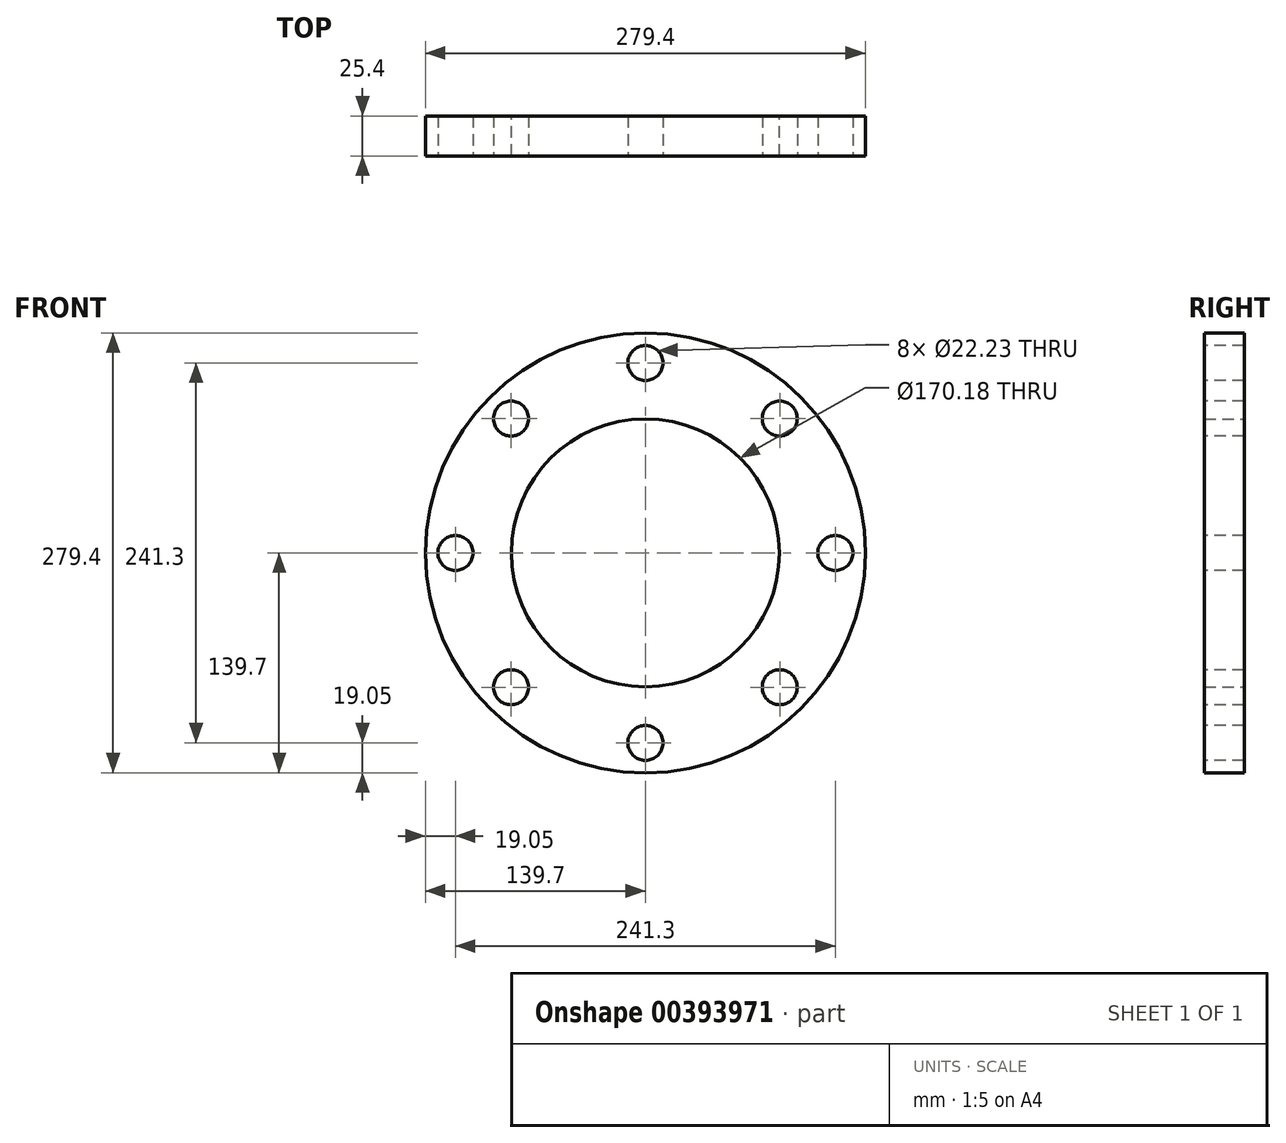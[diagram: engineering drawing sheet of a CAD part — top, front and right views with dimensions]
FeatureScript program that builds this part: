
annotation { "Feature Type Name" : "Feature", "Feature Type Description" : "" }
export const myFeature = defineFeature(function(context is Context, id is Id, definition is map)
    precondition{}
    {
        {
            var Q0;
            Q0=qCreatedBy(makeId("Front.planeOp"),FACE);
            var sketch = newSketch(context, id + "F0", { "sketchPlane" : qUnion([Q0])});
            skCircle(sketch, "E0", {"center": v(0, 0) * mm, "radius": 139.7 * mm});
            skCircle(sketch, "E1", {"center": v(0, 0) * mm, "radius": 85.1 * mm});
            skSolve(sketch);
        }
        {
            var Q0;
            Q0 = qSketchRegion(id + "F0", true);
            extrude(context, id + "F1", {"entities" : qUnion([Q0]), "depth" : 25.4 * mm});
        }
        {
            var Q0;
            Q0=makeQuery(id+"F1.opExtrude","CAP_FACE",FACE,{"disambiguationData":[OSD([sQuery(id+"F0.wireOp",EDGE,"E0"),sQuery(id+"F0.wireOp",EDGE,"E1")])],"isStart":false});
            var sketch = newSketch(context, id + "F2", { "sketchPlane" : qUnion([Q0])});
            skPoint(sketch, "E2", {"position": v(0, 120.65) * mm});
            skCircle(sketch, "E3", {"center": v(0, 0) * mm, "radius": 120.65 * mm, "construction": true});
            skPoint(sketch, "E4", {"position": v(-120.65, 0) * mm});
            skPoint(sketch, "E5", {"position": v(0, -120.65) * mm});
            skPoint(sketch, "E6", {"position": v(120.65, 0) * mm});
            skPoint(sketch, "E7", {"position": v(85.31, -85.31) * mm});
            skPoint(sketch, "E8", {"position": v(-85.31, -85.31) * mm});
            skPoint(sketch, "E9", {"position": v(-85.31, 85.31) * mm});
            skLineSegment(sketch, "E10", {"start": v(0, 0) * mm, "end": v(-124.95, -124.95) * mm, "construction": true});
            skPoint(sketch, "E11", {"position": v(85.31, 85.31) * mm});
            skSolve(sketch);
        }
        {
            var Q0;
            Q0=sQuery(id+"F2.wireOp",VERTEX,"E9");
            var Q1;
            Q1=sQuery(id+"F2.wireOp",VERTEX,"E2");
            var Q2;
            Q2=sQuery(id+"F2.wireOp",VERTEX,"E11");
            var Q3;
            Q3=sQuery(id+"F2.wireOp",VERTEX,"E6");
            var Q4;
            Q4=sQuery(id+"F2.wireOp",VERTEX,"E7");
            var Q5;
            Q5=sQuery(id+"F2.wireOp",VERTEX,"E5");
            var Q6;
            Q6=sQuery(id+"F2.wireOp",VERTEX,"E8");
            var Q7;
            Q7=sQuery(id+"F2.wireOp",VERTEX,"E4");
            var Q8;
            Q8=makeQuery(id+"F1.opExtrude","SWEPT_BODY",BODY,{"disambiguationData":[OSD([sQuery(id+"F0.wireOp",EDGE,"E0"),sQuery(id+"F0.wireOp",EDGE,"E1")])]});
            hole(context, id + "F3", {"style" : HoleStyle.SIMPLE, "endStyle" : HoleEndStyle.THROUGH, "holeDiameter" : 22.22 * mm, "isTappedThrough" : true, "tappedDepth" : 12.7 * mm, "tapClearance" : 3, "locations" : qUnion([Q0, Q1, Q2, Q3, Q4, Q5, Q6, Q7]), "scope" : qUnion([Q8])});
        }
    });
